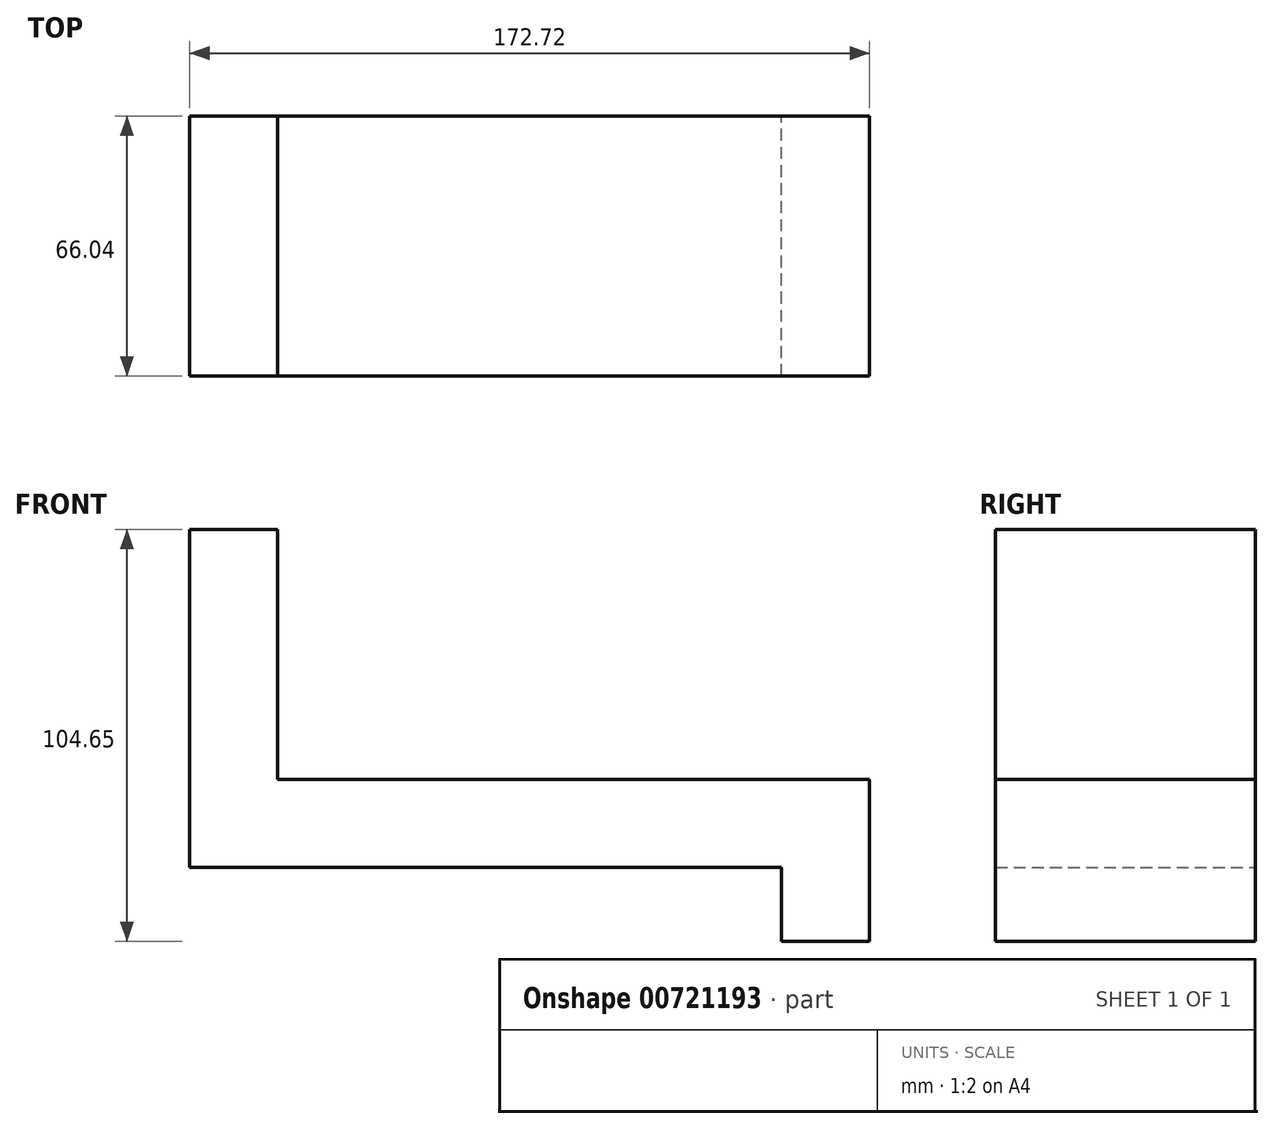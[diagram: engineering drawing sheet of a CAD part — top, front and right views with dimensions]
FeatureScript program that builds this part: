
annotation { "Feature Type Name" : "Feature", "Feature Type Description" : "" }
export const myFeature = defineFeature(function(context is Context, id is Id, definition is map)
    precondition{}
    {
        {
            var Q0;
            Q0=qCreatedBy(makeId("Front.planeOp"),FACE);
            var sketch = newSketch(context, id + "F0", { "sketchPlane" : qUnion([Q0])});
            skLineSegment(sketch, "E0.bottom", {"start": v(76.64, -61.9) * mm, "end": v(-73.73, -61.9) * mm});
            skLineSegment(sketch, "E0.top", {"start": v(54.29, -84.25) * mm, "end": v(-96.08, -84.25) * mm});
            skLineSegment(sketch, "E0.right", {"start": v(-96.08, -61.9) * mm, "end": v(-96.08, -84.25) * mm});
            skPoint(sketch, "E1", {"position": v(-73.73, -61.9) * mm});
            skLineSegment(sketch, "E2", {"start": v(-96.08, -61.9) * mm, "end": v(-96.08, 1.6) * mm});
            skLineSegment(sketch, "E3", {"start": v(-73.73, -61.9) * mm, "end": v(-73.73, 1.6) * mm});
            skLineSegment(sketch, "E4", {"start": v(-73.73, 1.6) * mm, "end": v(-96.08, 1.6) * mm});
            skPoint(sketch, "E5", {"position": v(54.29, -84.25) * mm});
            skLineSegment(sketch, "E6", {"start": v(54.29, -103.05) * mm, "end": v(54.29, -84.25) * mm});
            skLineSegment(sketch, "E7", {"start": v(54.29, -103.05) * mm, "end": v(76.64, -103.05) * mm});
            skPoint(sketch, "E0.left.end.orphan", {"position": v(76.64, -84.25) * mm});
            skLineSegment(sketch, "E8", {"start": v(76.64, -103.05) * mm, "end": v(76.64, -61.9) * mm});
            skSolve(sketch);
        }
        {
            var Q0;
            Q0 = qSketchRegion(id + "F0", true);
            extrude(context, id + "F1", {"entities" : qUnion([Q0]), "depth" : 66.04 * mm, "offsetDistance" : 25.4 * mm});
        }
    });
